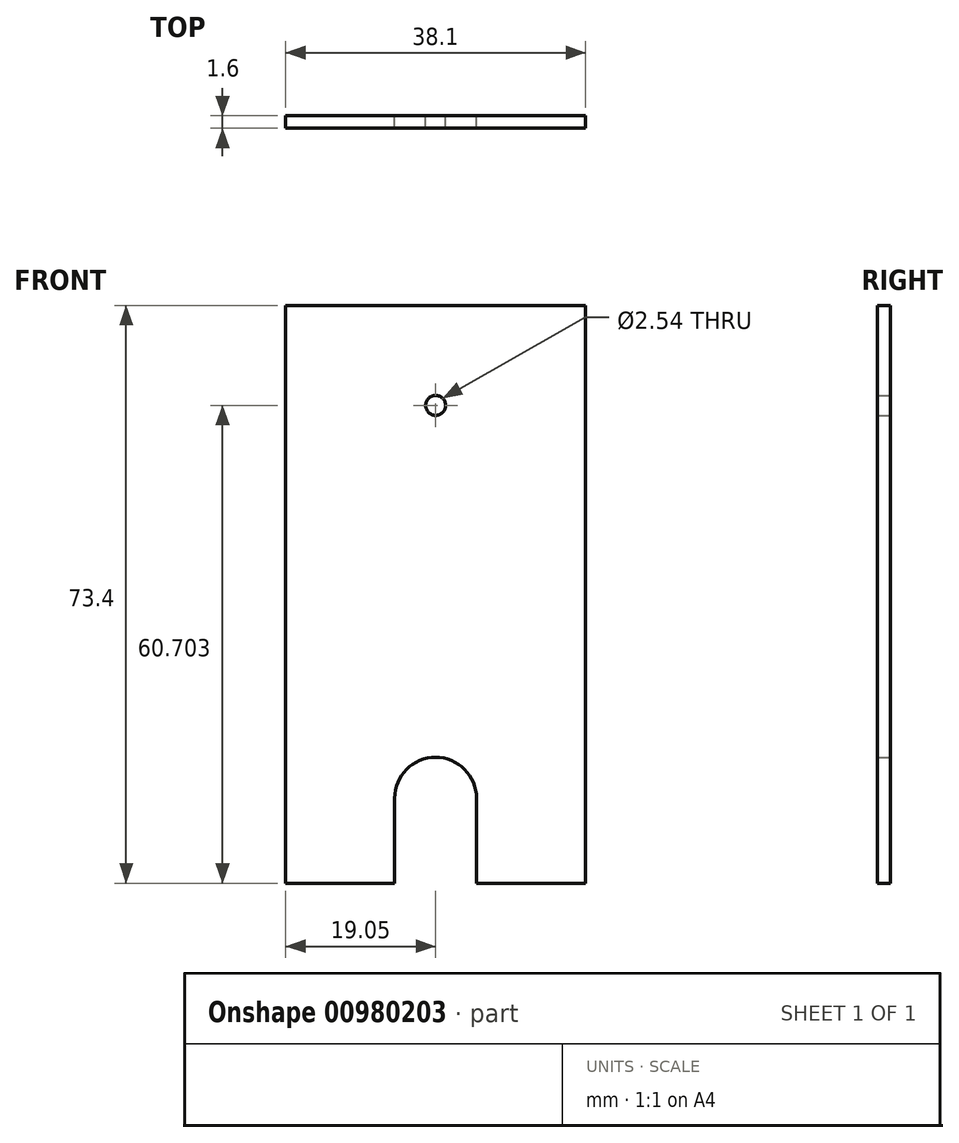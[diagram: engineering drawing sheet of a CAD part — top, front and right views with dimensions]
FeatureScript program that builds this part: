
annotation { "Feature Type Name" : "Feature", "Feature Type Description" : "" }
export const myFeature = defineFeature(function(context is Context, id is Id, definition is map)
    precondition{}
    {
        {
            var Q0;
            Q0=qCreatedBy(makeId("Front.planeOp"),FACE);
            var sketch = newSketch(context, id + "F0", { "sketchPlane" : qUnion([Q0])});
            skLineSegment(sketch, "E0", {"start": v(19.05, -36.7) * mm, "end": v(19.05, 36.7) * mm});
            skLineSegment(sketch, "E1", {"start": v(19.05, 36.7) * mm, "end": v(-19.05, 36.7) * mm});
            skLineSegment(sketch, "E2", {"start": v(-19.05, 36.7) * mm, "end": v(-19.05, -36.7) * mm});
            skLineSegment(sketch, "E3", {"start": v(-19.05, -36.7) * mm, "end": v(-5.2, -36.7) * mm});
            skLineSegment(sketch, "E4", {"start": v(-5.2, -36.7) * mm, "end": v(-5.2, -25.9) * mm});
            skArc(sketch, "E5", {"start": v(5.2, -25.9) * mm, "mid": v(0, -20.7) * mm, "end": v(-5.2, -25.9) * mm});
            skLineSegment(sketch, "E6", {"start": v(5.2, -25.9) * mm, "end": v(5.2, -36.7) * mm});
            skLineSegment(sketch, "E7", {"start": v(5.2, -36.7) * mm, "end": v(19.05, -36.7) * mm});
            skCircle(sketch, "E8", {"center": v(0, 24) * mm, "radius": 1.27 * mm});
            skSolve(sketch);
        }
        {
            var Q0;
            Q0=makeQuery(id+"F0.imprint","IMPRINT",FACE,{"disambiguationData":[TD([[makeQuery(id+"F0.imprint","IMPRINT",EDGE,{"derivedFrom":sQuery(id+"F0.wireOp",EDGE,"E0")}),1.0]])]});
            extrude(context, id + "F1", {"entities" : qUnion([Q0]), "depth" : 1.6 * mm, "offsetDistance" : 25.4 * mm});
        }
    });
